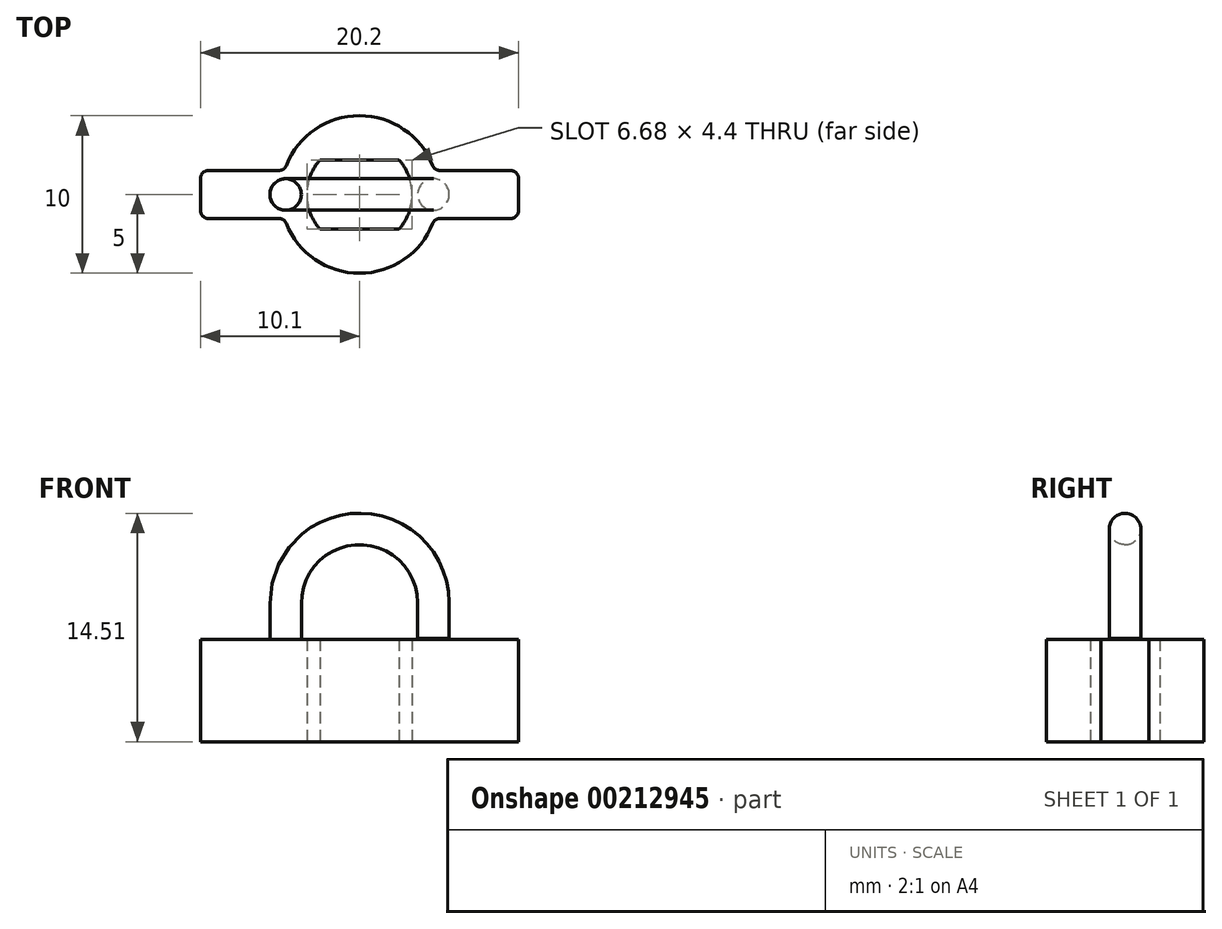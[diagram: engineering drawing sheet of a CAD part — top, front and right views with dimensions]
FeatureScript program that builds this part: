
annotation { "Feature Type Name" : "Feature", "Feature Type Description" : "" }
export const myFeature = defineFeature(function(context is Context, id is Id, definition is map)
    precondition{}
    {
        {
            var Q0;
            Q0=qCreatedBy(makeId("Top.planeOp"),FACE);
            var sketch = newSketch(context, id + "F0", { "sketchPlane" : qUnion([Q0])});
            skArc(sketch, "E0", {"start": v(-4.65, -1.84) * mm, "mid": v(0, -5) * mm, "end": v(4.65, -1.84) * mm});
            skLineSegment(sketch, "E1.right", {"start": v(-10.1, -1.02) * mm, "end": v(-10.1, 1.03) * mm});
            skLineSegment(sketch, "E2.bottom", {"start": v(5.11, -1.52) * mm, "end": v(9.6, -1.52) * mm});
            skLineSegment(sketch, "E2.top", {"start": v(5.11, 1.52) * mm, "end": v(9.6, 1.53) * mm});
            skLineSegment(sketch, "E2.right", {"start": v(10.1, -1.02) * mm, "end": v(10.1, 1.03) * mm});
            skPoint(sketch, "E3", {"position": v(-4.76, -1.52) * mm});
            skPoint(sketch, "E4", {"position": v(-4.76, 1.52) * mm});
            skPoint(sketch, "E5", {"position": v(4.76, 1.52) * mm});
            skPoint(sketch, "E6", {"position": v(4.76, -1.52) * mm});
            skPoint(sketch, "E7", {"position": v(10.1, 0) * mm});
            skPoint(sketch, "E8", {"position": v(-10.1, 0) * mm});
            skLineSegment(sketch, "E9.trimOffspring", {"start": v(-5.11, -1.52) * mm, "end": v(-9.6, -1.53) * mm});
            skLineSegment(sketch, "E10.trimOffspring", {"start": v(-5.11, 1.52) * mm, "end": v(-9.6, 1.52) * mm});
            skLineSegment(sketch, "E11", {"start": v(-10.1, 0) * mm, "end": v(0, 0) * mm, "construction": true});
            skLineSegment(sketch, "E12", {"start": v(10.1, 0) * mm, "end": v(0, 0) * mm, "construction": true});
            skArc(sketch, "E13.trimOffspring", {"start": v(4.65, 1.84) * mm, "mid": v(0, 5) * mm, "end": v(-4.65, 1.84) * mm});
            skArc(sketch, "E14.filletArc", {"start": v(-4.65, -1.84) * mm, "mid": v(-4.83, -1.61) * mm, "end": v(-5.11, -1.52) * mm});
            skArc(sketch, "E15.filletArc", {"start": v(5.11, -1.52) * mm, "mid": v(4.83, -1.61) * mm, "end": v(4.65, -1.84) * mm});
            skArc(sketch, "E16.filletArc", {"start": v(4.65, 1.84) * mm, "mid": v(4.83, 1.61) * mm, "end": v(5.11, 1.52) * mm});
            skArc(sketch, "E17.filletArc", {"start": v(-5.11, 1.52) * mm, "mid": v(-4.83, 1.61) * mm, "end": v(-4.65, 1.84) * mm});
            skPoint(sketch, "E18.visualSharp", {"position": v(-10.1, 1.53) * mm});
            skArc(sketch, "E18.filletArc", {"start": v(-9.6, 1.53) * mm, "mid": v(-9.95, 1.38) * mm, "end": v(-10.1, 1.03) * mm});
            skPoint(sketch, "E19.visualSharp", {"position": v(-10.1, -1.52) * mm});
            skArc(sketch, "E19.filletArc", {"start": v(-10.1, -1.02) * mm, "mid": v(-9.95, -1.38) * mm, "end": v(-9.6, -1.53) * mm});
            skPoint(sketch, "E20.visualSharp", {"position": v(10.1, -1.52) * mm});
            skArc(sketch, "E20.filletArc", {"start": v(9.6, -1.52) * mm, "mid": v(9.95, -1.38) * mm, "end": v(10.1, -1.02) * mm});
            skPoint(sketch, "E21.visualSharp", {"position": v(10.1, 1.53) * mm});
            skArc(sketch, "E21.filletArc", {"start": v(10.1, 1.03) * mm, "mid": v(9.95, 1.38) * mm, "end": v(9.6, 1.52) * mm});
            skSolve(sketch);
        }
        {
            var Q0;
            Q0=qCreatedBy(makeId("Top.planeOp"),FACE);
            var sketch = newSketch(context, id + "F1", { "sketchPlane" : qUnion([Q0])});
            skArc(sketch, "E22", {"start": v(-2.51, 2.2) * mm, "mid": v(-3.34, 0) * mm, "end": v(-2.51, -2.2) * mm});
            skLineSegment(sketch, "E23", {"start": v(-2.51, -2.2) * mm, "end": v(2.51, -2.2) * mm});
            skLineSegment(sketch, "E24", {"start": v(-2.51, 2.2) * mm, "end": v(2.51, 2.2) * mm});
            skArc(sketch, "E25.trimOffspring", {"start": v(2.51, -2.2) * mm, "mid": v(3.34, 0) * mm, "end": v(2.51, 2.2) * mm});
            skSolve(sketch);
        }
        {
            var Q0;
            Q0 = qSketchRegion(id + "F0", true);
            extrude(context, id + "F2", {"entities" : qUnion([Q0]), "depth" : 6.5 * mm});
        }
        {
            var Q0;
            Q0 = qSketchRegion(id + "F1", true);
            extrude(context, id + "F3", {"entities" : qUnion([Q0]), "operationType" : NewBodyOperationType.REMOVE, "endBound" : BoundingType.THROUGH_ALL, "depth" : 11.9 * mm});
        }
        {
            var Q0;
            Q0=qCreatedBy(makeId("Front.planeOp"),FACE);
            var sketch = newSketch(context, id + "F4", { "sketchPlane" : qUnion([Q0])});
            skArc(sketch, "E26", {"start": v(4.36, 8.82) * mm, "mid": v(0, 13.18) * mm, "end": v(-4.36, 8.82) * mm});
            skLineSegment(sketch, "E27", {"start": v(0, 8.82) * mm, "end": v(-4.36, 8.82) * mm, "construction": true});
            skLineSegment(sketch, "E28", {"start": v(0, 8.82) * mm, "end": v(4.36, 8.82) * mm, "construction": true});
            skLineSegment(sketch, "E29", {"start": v(-4.36, 8.82) * mm, "end": v(-4.36, 6.54) * mm});
            skLineSegment(sketch, "E30", {"start": v(4.36, 8.82) * mm, "end": v(4.36, 6.54) * mm});
            skSolve(sketch);
        }
        {
            var Q0;
            Q0=makeQuery(id+"F2.opExtrude","CAP_FACE",FACE,{"disambiguationData":[OSD([sQuery(id+"F0.wireOp",EDGE,"E0"),sQuery(id+"F0.wireOp",EDGE,"E1.right"),sQuery(id+"F0.wireOp",EDGE,"E2.bottom"),sQuery(id+"F0.wireOp",EDGE,"E2.top"),sQuery(id+"F0.wireOp",EDGE,"E2.right"),sQuery(id+"F0.wireOp",EDGE,"E9.trimOffspring"),sQuery(id+"F0.wireOp",EDGE,"E10.trimOffspring")])],"isStart":false});
            var sketch = newSketch(context, id + "F5", { "sketchPlane" : qUnion([Q0])});
            skCircle(sketch, "E31", {"center": v(-4.7, 0) * mm, "radius": 1 * mm});
            skSolve(sketch);
        }
        {
            var Q0;
            Q0=makeQuery(id+"F5.imprint","IMPRINT",FACE,{"disambiguationData":[TD([[makeQuery(id+"F5.imprint","IMPRINT",EDGE,{"derivedFrom":sQuery(id+"F5.wireOp",EDGE,"E31")}),1.0]])]});
            var Q1;
            Q1=sQuery(id+"F4.wireOp",EDGE,"E29");
            var Q2;
            Q2=sQuery(id+"F4.wireOp",EDGE,"E26");
            var Q3;
            Q3=sQuery(id+"F4.wireOp",EDGE,"E30");
            sweep(context, id + "F6", {"operationType" : NewBodyOperationType.ADD, "profiles" : qUnion([Q0]), "path" : qUnion([Q1, Q2, Q3])});
        }
    });
